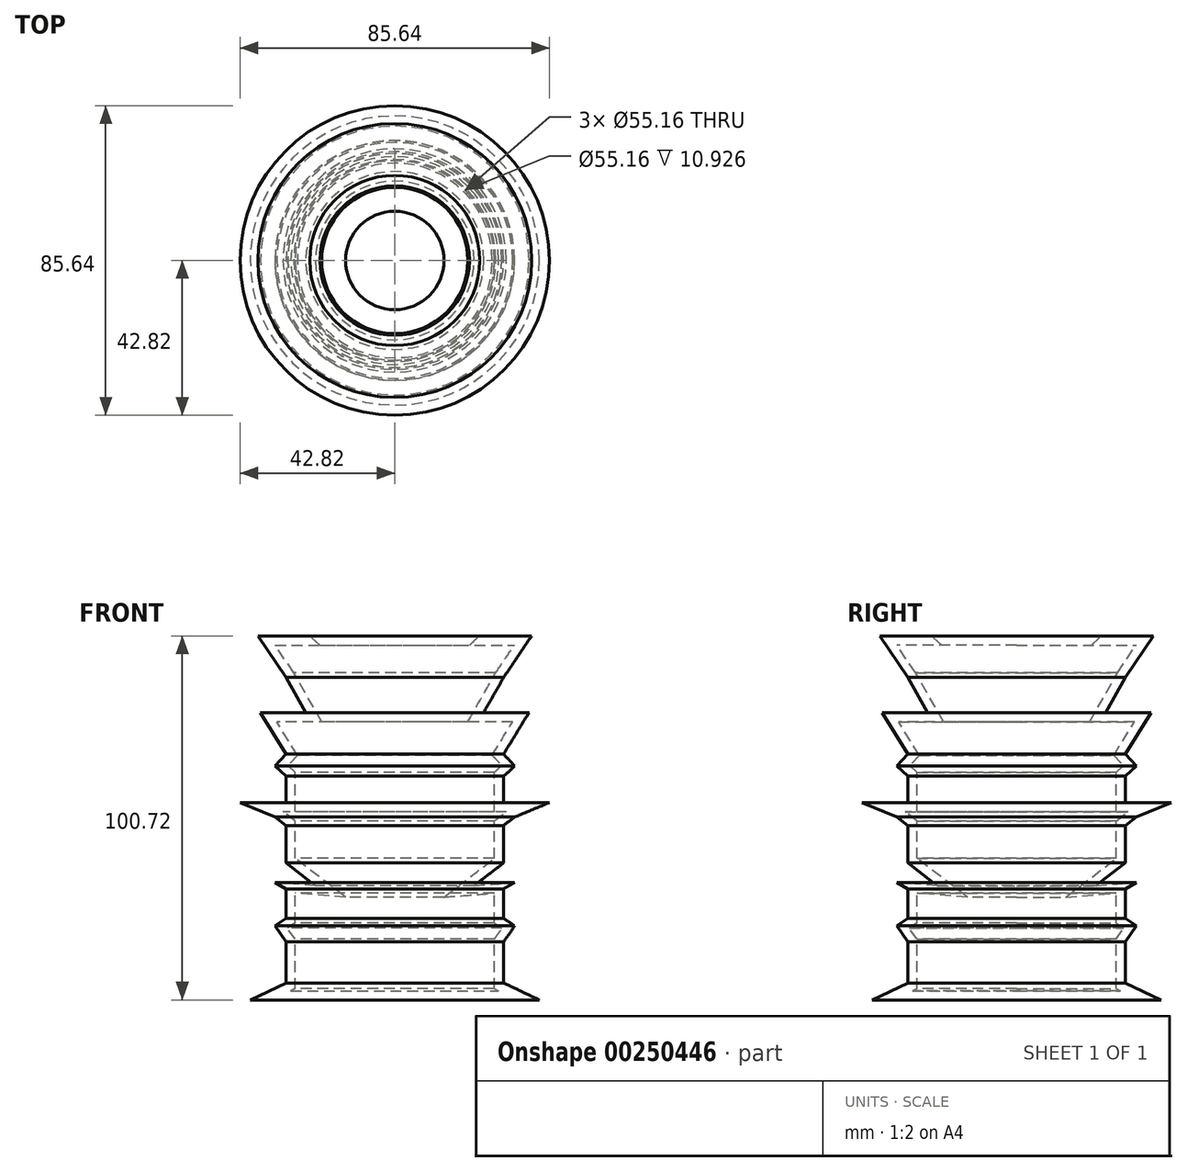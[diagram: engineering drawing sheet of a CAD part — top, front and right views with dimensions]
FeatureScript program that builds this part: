
annotation { "Feature Type Name" : "Feature", "Feature Type Description" : "" }
export const myFeature = defineFeature(function(context is Context, id is Id, definition is map)
    precondition{}
    {
        {
            var Q0;
            Q0=qCreatedBy(makeId("Front.planeOp"),FACE);
            var sketch = newSketch(context, id + "F0", { "sketchPlane" : qUnion([Q0])});
            skLineSegment(sketch, "E0", {"start": v(-37.89, 52) * mm, "end": v(-30.12, 40.48) * mm});
            skLineSegment(sketch, "E1", {"start": v(-30.12, 19.3) * mm, "end": v(-33.18, 16) * mm});
            skLineSegment(sketch, "E2", {"start": v(-33.18, 16) * mm, "end": v(-30.12, 13.16) * mm});
            skLineSegment(sketch, "E3", {"start": v(-30.12, 13.16) * mm, "end": v(-30.12, 5.88) * mm});
            skLineSegment(sketch, "E4", {"start": v(-33.18, 1.88) * mm, "end": v(-30.12, -0.46) * mm});
            skLineSegment(sketch, "E5", {"start": v(-30.12, -0.46) * mm, "end": v(-30.12, -10.82) * mm});
            skLineSegment(sketch, "E6", {"start": v(-33.18, -16.24) * mm, "end": v(-30.12, -17.97) * mm});
            skLineSegment(sketch, "E7", {"start": v(-30.12, -17.97) * mm, "end": v(-30.12, -26.12) * mm});
            skLineSegment(sketch, "E8", {"start": v(-30.12, -26.12) * mm, "end": v(-33.18, -28.24) * mm});
            skLineSegment(sketch, "E9", {"start": v(-33.18, -28.24) * mm, "end": v(-30.12, -32.66) * mm});
            skLineSegment(sketch, "E10", {"start": v(-30.12, -32.66) * mm, "end": v(-30.12, -44) * mm});
            skLineSegment(sketch, "E11", {"start": v(-30.12, -44) * mm, "end": v(-40, -48.71) * mm});
            skLineSegment(sketch, "E12", {"start": v(-40, -48.71) * mm, "end": v(0, -48.71) * mm});
            skLineSegment(sketch, "E13", {"start": v(0, -48.71) * mm, "end": v(0, 52) * mm});
            skLineSegment(sketch, "E14", {"start": v(0, 73.66) * mm, "end": v(0, -61.9) * mm, "construction": true});
            skLineSegment(sketch, "E15", {"start": v(-37.89, 52) * mm, "end": v(-23.53, 52) * mm});
            skLineSegment(sketch, "E16", {"start": v(-23.53, 52) * mm, "end": v(-19.3, 48.24) * mm});
            skLineSegment(sketch, "E17", {"start": v(-19.3, 48.24) * mm, "end": v(0, 48.24) * mm});
            skLineSegment(sketch, "E18", {"start": v(-30.12, 40.48) * mm, "end": v(-24.6, 30.79) * mm});
            skLineSegment(sketch, "E19", {"start": v(-24.6, 30.79) * mm, "end": v(-37.17, 30.79) * mm});
            skLineSegment(sketch, "E20", {"start": v(-37.17, 30.79) * mm, "end": v(-30.12, 19.3) * mm});
            skLineSegment(sketch, "E21", {"start": v(-30.12, 5.88) * mm, "end": v(-42.82, 5.88) * mm});
            skLineSegment(sketch, "E22", {"start": v(-42.82, 5.88) * mm, "end": v(-33.18, 1.88) * mm});
            skLineSegment(sketch, "E23", {"start": v(-30.12, -10.82) * mm, "end": v(-21.94, -17.08) * mm});
            skLineSegment(sketch, "E24", {"start": v(-21.94, -17.08) * mm, "end": v(-33.18, -16.24) * mm});
            skSolve(sketch);
        }
        {
            var Q0;
            Q0=makeQuery(id+"F0.imprint","IMPRINT",FACE,{"disambiguationData":[TD([[makeQuery(id+"F0.imprint","IMPRINT",EDGE,{"derivedFrom":sQuery(id+"F0.wireOp",EDGE,"E0")}),1.0]])]});
            var Q1;
            Q1=sQuery(id+"F0.wireOp",EDGE,"E14");
            revolve(context, id + "F1", {"entities" : qUnion([Q0]), "axis" : qUnion([Q1]), "revolveType" : RevolveType.FULL});
        }
        {
            var Q0;
            Q0=makeQuery(id+"F1.opRevolve","SWEPT_FACE",FACE,{"disambiguationData":[OSD([sQuery(id+"F0.wireOp",EDGE,"E17")])]});
            var Q1;
            Q1=makeQuery(id+"F1.opRevolve","SWEPT_FACE",FACE,{"disambiguationData":[OSD([sQuery(id+"F0.wireOp",EDGE,"E16")])]});
            shell(context, id + "F2", {"entities" : qUnion([Q0, Q1]), "thickness" : 2.54 * mm});
        }
    });
